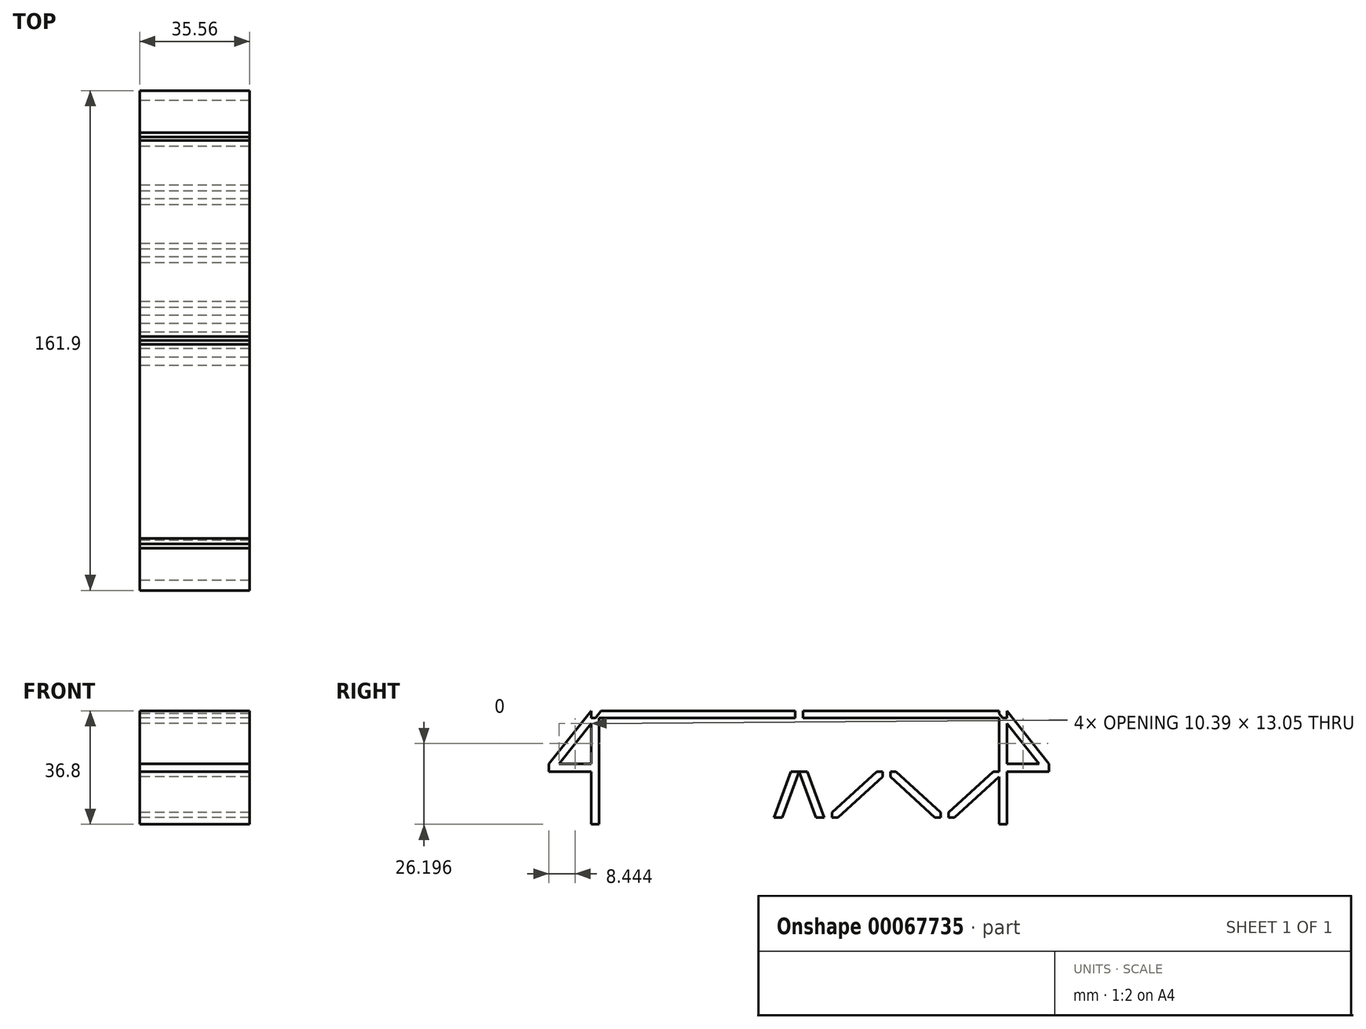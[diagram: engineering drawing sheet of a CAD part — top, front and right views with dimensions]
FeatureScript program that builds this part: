
annotation { "Feature Type Name" : "Feature", "Feature Type Description" : "" }
export const myFeature = defineFeature(function(context is Context, id is Id, definition is map)
    precondition{}
    {
        {
            var Q0;
            Q0=qCreatedBy(makeId("Right.planeOp"),FACE);
            var sketch = newSketch(context, id + "F0", { "sketchPlane" : qUnion([Q0])});
            skLineSegment(sketch, "E0.bottom", {"start": v(-67.31, 18.4) * mm, "end": v(67.3, 18.4) * mm});
            skLineSegment(sketch, "E0.top", {"start": v(-80.95, -18.4) * mm, "end": v(80.95, -18.4) * mm});
            skLineSegment(sketch, "E0.left", {"start": v(-80.95, 1.27) * mm, "end": v(-80.95, -18.4) * mm});
            skLineSegment(sketch, "E0.right", {"start": v(80.95, 1.27) * mm, "end": v(80.95, -18.4) * mm});
            skLineSegment(sketch, "E1.1", {"start": v(-78.4, 4.46) * mm, "end": v(-78.4, -16.22) * mm});
            skLineSegment(sketch, "E1.2", {"start": v(-78.4, -16.22) * mm, "end": v(78.4, -16.22) * mm});
            skLineSegment(sketch, "E1.3", {"start": v(78.4, 4.46) * mm, "end": v(78.4, -16.22) * mm});
            skLineSegment(sketch, "E2.rect.bottom", {"start": v(80.95, 1.27) * mm, "end": v(-80.95, 1.27) * mm});
            skLineSegment(sketch, "E2.rect.top", {"start": v(80.95, -1.27) * mm, "end": v(-80.95, -1.27) * mm});
            skLineSegment(sketch, "E2.rect.left", {"start": v(80.95, 1.27) * mm, "end": v(80.95, -1.27) * mm});
            skLineSegment(sketch, "E2.rect.right", {"start": v(-80.95, 1.27) * mm, "end": v(-80.95, -1.27) * mm});
            skPoint(sketch, "E2.rect.middle", {"position": v(0, 0) * mm});
            skLineSegment(sketch, "E3.rect.bottom", {"start": v(1.27, 18.4) * mm, "end": v(-1.27, 18.4) * mm});
            skLineSegment(sketch, "E3.rect.top", {"start": v(1.27, 1.27) * mm, "end": v(-1.27, 1.27) * mm});
            skLineSegment(sketch, "E3.rect.left", {"start": v(1.27, 18.4) * mm, "end": v(1.27, 1.27) * mm});
            skLineSegment(sketch, "E3.rect.right", {"start": v(-1.27, 18.4) * mm, "end": v(-1.27, 1.27) * mm});
            skPoint(sketch, "E3.rect.middle", {"position": v(0, 9.83) * mm});
            skPoint(sketch, "E3.rect.middle.positionSnap0", {"position": v(0, 1.27) * mm});
            skPoint(sketch, "E3.rect.centerSnap0", {"position": v(0, 1.27) * mm});
            skLineSegment(sketch, "E4.rect.bottom", {"start": v(67.3, 18.4) * mm, "end": v(64.77, 18.4) * mm});
            skLineSegment(sketch, "E4.rect.top", {"start": v(67.3, -18.4) * mm, "end": v(64.77, -18.4) * mm});
            skLineSegment(sketch, "E4.rect.left", {"start": v(67.3, 18.4) * mm, "end": v(67.3, -18.4) * mm});
            skLineSegment(sketch, "E4.rect.right", {"start": v(64.77, 18.4) * mm, "end": v(64.77, -18.4) * mm});
            skPoint(sketch, "E4.rect.middle", {"position": v(66.04, 0) * mm});
            skLineSegment(sketch, "E5.rect.bottom", {"start": v(-64.77, 18.4) * mm, "end": v(-67.31, 18.4) * mm});
            skLineSegment(sketch, "E5.rect.top", {"start": v(-64.77, -18.4) * mm, "end": v(-67.31, -18.4) * mm});
            skLineSegment(sketch, "E5.rect.left", {"start": v(-64.77, 18.4) * mm, "end": v(-64.77, -18.4) * mm});
            skLineSegment(sketch, "E5.rect.right", {"start": v(-67.31, 18.4) * mm, "end": v(-67.31, -18.4) * mm});
            skPoint(sketch, "E5.rect.middle", {"position": v(-66.04, 0) * mm});
            skLineSegment(sketch, "E6.bottom", {"start": v(-48.44, -1.27) * mm, "end": v(-45.9, -1.27) * mm});
            skLineSegment(sketch, "E6.top", {"start": v(-48.44, -16.22) * mm, "end": v(-45.9, -16.22) * mm});
            skLineSegment(sketch, "E6.left", {"start": v(-48.44, -1.27) * mm, "end": v(-48.44, -16.22) * mm});
            skLineSegment(sketch, "E6.right", {"start": v(-45.9, -1.27) * mm, "end": v(-45.9, -16.22) * mm});
            skLineSegment(sketch, "E7.bottom", {"start": v(-29.57, -1.27) * mm, "end": v(-27.03, -1.27) * mm});
            skLineSegment(sketch, "E7.top", {"start": v(-29.57, -16.22) * mm, "end": v(-27.03, -16.22) * mm});
            skLineSegment(sketch, "E7.left", {"start": v(-29.57, -1.27) * mm, "end": v(-29.57, -16.22) * mm});
            skLineSegment(sketch, "E7.right", {"start": v(-27.03, -1.27) * mm, "end": v(-27.03, -16.22) * mm});
            skLineSegment(sketch, "E8.bottom", {"start": v(-10.7, -1.27) * mm, "end": v(-8.15, -1.27) * mm});
            skLineSegment(sketch, "E8.top", {"start": v(-10.7, -16.22) * mm, "end": v(-8.15, -16.22) * mm});
            skLineSegment(sketch, "E8.left", {"start": v(-10.7, -1.27) * mm, "end": v(-10.7, -16.22) * mm});
            skLineSegment(sketch, "E8.right", {"start": v(-8.15, -1.27) * mm, "end": v(-8.15, -16.22) * mm});
            skLineSegment(sketch, "E9.bottom", {"start": v(8.15, -1.27) * mm, "end": v(10.7, -1.27) * mm});
            skLineSegment(sketch, "E9.top", {"start": v(8.15, -16.22) * mm, "end": v(10.7, -16.22) * mm});
            skLineSegment(sketch, "E9.left", {"start": v(8.15, -1.27) * mm, "end": v(8.15, -16.22) * mm});
            skLineSegment(sketch, "E9.right", {"start": v(10.7, -1.27) * mm, "end": v(10.7, -16.22) * mm});
            skLineSegment(sketch, "E10.bottom", {"start": v(27.03, -1.27) * mm, "end": v(29.57, -1.27) * mm});
            skLineSegment(sketch, "E10.top", {"start": v(27.03, -16.22) * mm, "end": v(29.57, -16.22) * mm});
            skLineSegment(sketch, "E10.left", {"start": v(27.03, -1.27) * mm, "end": v(27.03, -16.22) * mm});
            skLineSegment(sketch, "E10.right", {"start": v(29.57, -1.27) * mm, "end": v(29.57, -16.22) * mm});
            skLineSegment(sketch, "E11.bottom", {"start": v(45.9, -1.27) * mm, "end": v(48.44, -1.27) * mm});
            skLineSegment(sketch, "E11.top", {"start": v(45.9, -16.22) * mm, "end": v(48.44, -16.22) * mm});
            skLineSegment(sketch, "E11.left", {"start": v(45.9, -1.27) * mm, "end": v(45.9, -16.22) * mm});
            skLineSegment(sketch, "E11.right", {"start": v(48.44, -1.27) * mm, "end": v(48.44, -16.22) * mm});
            skLineSegment(sketch, "E12", {"start": v(0, 19.15) * mm, "end": v(0, -18.4) * mm, "construction": true});
            skLineSegment(sketch, "E13", {"start": v(-80.95, 0.2) * mm, "end": v(80.95, 0.2) * mm, "construction": true});
            skLineSegment(sketch, "E14", {"start": v(67.31, 18.4) * mm, "end": v(80.95, 1.27) * mm});
            skLineSegment(sketch, "E15", {"start": v(64.06, 18.4) * mm, "end": v(79.73, -1.27) * mm});
            skLineSegment(sketch, "E16", {"start": v(-67.31, 18.4) * mm, "end": v(-80.95, 1.27) * mm});
            skLineSegment(sketch, "E17", {"start": v(-64.06, 18.4) * mm, "end": v(-79.73, -1.27) * mm});
            skLineSegment(sketch, "E18.trimOffspring", {"start": v(-69.13, 16.12) * mm, "end": v(67.3, 16.12) * mm});
            skLineSegment(sketch, "E19", {"start": v(0, -1.27) * mm, "end": v(-5.45, -16.22) * mm});
            skLineSegment(sketch, "E20", {"start": v(-2.7, -1.27) * mm, "end": v(-8.15, -16.22) * mm});
            skLineSegment(sketch, "E21", {"start": v(0, -1.27) * mm, "end": v(5.45, -16.22) * mm});
            skLineSegment(sketch, "E22", {"start": v(2.7, -1.27) * mm, "end": v(8.15, -16.22) * mm});
            skLineSegment(sketch, "E23.0", {"start": v(27.03, -3) * mm, "end": v(12.57, -16.22) * mm});
            skLineSegment(sketch, "E24.0", {"start": v(25.14, -1.27) * mm, "end": v(10.7, -14.5) * mm});
            skLineSegment(sketch, "E25.0", {"start": v(31.45, -1.27) * mm, "end": v(45.9, -14.5) * mm});
            skLineSegment(sketch, "E26.0", {"start": v(29.57, -3) * mm, "end": v(44.02, -16.22) * mm});
            skLineSegment(sketch, "E27.0", {"start": v(50.32, -16.22) * mm, "end": v(64.77, -3) * mm});
            skLineSegment(sketch, "E28.0", {"start": v(48.44, -14.5) * mm, "end": v(62.89, -1.27) * mm});
            skPoint(sketch, "E29.startSnap0", {"position": v(67.3, 0) * mm});
            skLineSegment(sketch, "E30.0", {"start": v(67.31, -3.4) * mm, "end": v(76.8, -16.22) * mm});
            skLineSegment(sketch, "E31.0", {"start": v(68.9, -1.27) * mm, "end": v(78.4, -14) * mm});
            skSolve(sketch);
        }
        {
            var Q0;
            {var subQ4=sQuery(id+"F0.wireOp",EDGE,"E27.0");Q0=makeQuery(id+"F0.imprint","IMPRINT",FACE,{"disambiguationData":[TD([[makeQuery(id+"F0.imprint","IMPRINT",EDGE,{"derivedFrom":subQ4}),1.0]])]});}
            var Q1;
            {var subQ2=sQuery(id+"F0.wireOp",EDGE,"E21");Q1=makeQuery(id+"F0.imprint","IMPRINT",FACE,{"disambiguationData":[TD([[makeQuery(id+"F0.imprint","IMPRINT",EDGE,{"derivedFrom":subQ2}),1.0]])]});}
            var Q2;
            {var subQ7=sQuery(id+"F0.wireOp",EDGE,"E0.right");Q2=makeQuery(id+"F0.imprint","IMPRINT",FACE,{"disambiguationData":[TD([[makeQuery(id+"F0.imprint","IMPRINT",EDGE,{"derivedFrom":subQ7}),-1.0]])]});}
            var Q3;
            Q3=makeQuery(id+"F0.imprint","IMPRINT",FACE,{"disambiguationData":[TD([[makeQuery(id+"F0.imprint","IMPRINT",EDGE,{"derivedFrom":sQuery(id+"F0.wireOp",EDGE,"E7.bottom")}),-1.0]])]});
            var Q4;
            {var subQ2=sQuery(id+"F0.wireOp",EDGE,"E19");Q4=makeQuery(id+"F0.imprint","IMPRINT",FACE,{"disambiguationData":[TD([[makeQuery(id+"F0.imprint","IMPRINT",EDGE,{"derivedFrom":subQ2}),-1.0]])]});}
            var Q5;
            {var subQ1=sQuery(id+"F0.wireOp",EDGE,"E1.3");var subQ8=sQuery(id+"F0.wireOp",EDGE,"E14");var subQ10=makeQuery(id+"F0.imprint","INTERSECT",VERTEX,{"derivedFrom":[subQ1,subQ8]});Q5=makeQuery(id+"F0.imprint","IMPRINT",FACE,{"disambiguationData":[TD([[makeQuery(id+"F0.imprint","IMPRINT",EDGE,{"disambiguationData":[TD([[subQ10,-1.0]])],"derivedFrom":subQ1}),-1.0]])]});}
            var Q6;
            {var subQ0=sQuery(id+"F0.wireOp",EDGE,"E16");var subQ1=sQuery(id+"F0.wireOp",EDGE,"E1.1");var subQ2=makeQuery(id+"F0.imprint","INTERSECT",VERTEX,{"derivedFrom":[subQ1,subQ0]});Q6=makeQuery(id+"F0.imprint","IMPRINT",FACE,{"disambiguationData":[TD([[makeQuery(id+"F0.imprint","IMPRINT",EDGE,{"disambiguationData":[TD([[subQ2,-1.0]])],"derivedFrom":subQ1}),1.0]])]});}
            var Q7;
            {var subQ7=sQuery(id+"F0.wireOp",EDGE,"E25.0");Q7=makeQuery(id+"F0.imprint","IMPRINT",FACE,{"disambiguationData":[TD([[makeQuery(id+"F0.imprint","IMPRINT",EDGE,{"derivedFrom":subQ7}),-1.0]])]});}
            var Q8;
            {var subQ0=sQuery(id+"F0.wireOp",EDGE,"E17");var subQ3=sQuery(id+"F0.wireOp",EDGE,"E5.rect.left");var subQ4=makeQuery(id+"F0.imprint","INTERSECT",VERTEX,{"derivedFrom":[subQ3,subQ0]});Q8=makeQuery(id+"F0.imprint","IMPRINT",FACE,{"disambiguationData":[TD([[makeQuery(id+"F0.imprint","IMPRINT",EDGE,{"disambiguationData":[TD([[subQ4,-1.0]])],"derivedFrom":subQ3}),1.0]])]});}
            var Q9;
            Q9=makeQuery(id+"F0.imprint","IMPRINT",FACE,{"disambiguationData":[TD([[makeQuery(id+"F0.imprint","IMPRINT",EDGE,{"derivedFrom":sQuery(id+"F0.wireOp",EDGE,"E8.bottom")}),-1.0]])]});
            var Q10;
            {var subQ0=sQuery(id+"F0.wireOp",EDGE,"E3.rect.top");Q10=makeQuery(id+"F0.imprint","IMPRINT",FACE,{"disambiguationData":[TD([[makeQuery(id+"F0.imprint","IMPRINT",EDGE,{"derivedFrom":subQ0}),-1.0]])]});}
            var Q11;
            {var subQ7=sQuery(id+"F0.wireOp",EDGE,"E0.left");Q11=makeQuery(id+"F0.imprint","IMPRINT",FACE,{"disambiguationData":[TD([[makeQuery(id+"F0.imprint","IMPRINT",EDGE,{"derivedFrom":subQ7}),1.0]])]});}
            var Q12;
            Q12=makeQuery(id+"F0.imprint","IMPRINT",FACE,{"disambiguationData":[TD([[makeQuery(id+"F0.imprint","IMPRINT",EDGE,{"derivedFrom":sQuery(id+"F0.wireOp",EDGE,"E6.bottom")}),-1.0]])]});
            var Q13;
            {var subQ15=sQuery(id+"F0.wireOp",EDGE,"E6.top");Q13=makeQuery(id+"F0.imprint","IMPRINT",FACE,{"disambiguationData":[TD([[makeQuery(id+"F0.imprint","IMPRINT",EDGE,{"derivedFrom":subQ15}),-1.0]])]});}
            var Q14;
            {var subQ1=sQuery(id+"F0.wireOp",EDGE,"E9.bottom");Q14=makeQuery(id+"F0.imprint","IMPRINT",FACE,{"disambiguationData":[TD([[makeQuery(id+"F0.imprint","IMPRINT",EDGE,{"derivedFrom":subQ1}),-1.0]])]});}
            var Q15;
            {var subQ4=sQuery(id+"F0.wireOp",EDGE,"E11.bottom");Q15=makeQuery(id+"F0.imprint","IMPRINT",FACE,{"disambiguationData":[TD([[makeQuery(id+"F0.imprint","IMPRINT",EDGE,{"derivedFrom":subQ4}),-1.0]])]});}
            var Q16;
            {var subQ0=sQuery(id+"F0.wireOp",EDGE,"E4.rect.right");var subQ5=sQuery(id+"F0.wireOp",EDGE,"E1.2");var subQ8=makeQuery(id+"F0.imprint","INTERSECT",VERTEX,{"derivedFrom":[subQ5,subQ0]});Q16=makeQuery(id+"F0.imprint","IMPRINT",FACE,{"disambiguationData":[TD([[makeQuery(id+"F0.imprint","IMPRINT",EDGE,{"disambiguationData":[TD([[subQ8,-1.0]])],"derivedFrom":subQ5}),1.0]])]});}
            var Q17;
            {var subQ5=sQuery(id+"F0.wireOp",EDGE,"E2.rect.bottom");var subQ7=sQuery(id+"F0.wireOp",EDGE,"E5.rect.left");var subQ8=makeQuery(id+"F0.imprint","INTERSECT",VERTEX,{"derivedFrom":[subQ5,subQ7]});Q17=makeQuery(id+"F0.imprint","IMPRINT",FACE,{"disambiguationData":[TD([[makeQuery(id+"F0.imprint","IMPRINT",EDGE,{"disambiguationData":[TD([[subQ8,-1.0]])],"derivedFrom":subQ5}),-1.0]])]});}
            var Q18;
            {var subQ0=sQuery(id+"F0.wireOp",EDGE,"E14");var subQ1=sQuery(id+"F0.wireOp",EDGE,"E1.3");var subQ2=makeQuery(id+"F0.imprint","INTERSECT",VERTEX,{"derivedFrom":[subQ1,subQ0]});Q18=makeQuery(id+"F0.imprint","IMPRINT",FACE,{"disambiguationData":[TD([[makeQuery(id+"F0.imprint","IMPRINT",EDGE,{"disambiguationData":[TD([[subQ2,-1.0]])],"derivedFrom":subQ1}),1.0]])]});}
            var Q19;
            {var subQ0=sQuery(id+"F0.wireOp",EDGE,"E16");var subQ1=sQuery(id+"F0.wireOp",EDGE,"E1.1");var subQ2=makeQuery(id+"F0.imprint","INTERSECT",VERTEX,{"derivedFrom":[subQ1,subQ0]});Q19=makeQuery(id+"F0.imprint","IMPRINT",FACE,{"disambiguationData":[TD([[makeQuery(id+"F0.imprint","IMPRINT",EDGE,{"disambiguationData":[TD([[subQ2,-1.0]])],"derivedFrom":subQ1}),-1.0]])]});}
            var Q20;
            {var subQ0=sQuery(id+"F0.wireOp",EDGE,"E5.rect.right");var subQ1=sQuery(id+"F0.wireOp",EDGE,"E1.2");var subQ2=makeQuery(id+"F0.imprint","INTERSECT",VERTEX,{"derivedFrom":[subQ1,subQ0]});Q20=makeQuery(id+"F0.imprint","IMPRINT",FACE,{"disambiguationData":[TD([[makeQuery(id+"F0.imprint","IMPRINT",EDGE,{"disambiguationData":[TD([[subQ2,-1.0]])],"derivedFrom":subQ1}),1.0]])]});}
            var Q21;
            {var subQ4=sQuery(id+"F0.wireOp",EDGE,"E10.bottom");Q21=makeQuery(id+"F0.imprint","IMPRINT",FACE,{"disambiguationData":[TD([[makeQuery(id+"F0.imprint","IMPRINT",EDGE,{"derivedFrom":subQ4}),-1.0]])]});}
            var Q22;
            {var subQ3=sQuery(id+"F0.wireOp",EDGE,"E23.0");Q22=makeQuery(id+"F0.imprint","IMPRINT",FACE,{"disambiguationData":[TD([[makeQuery(id+"F0.imprint","IMPRINT",EDGE,{"derivedFrom":subQ3}),-1.0]])]});}
            var Q23;
            {var subQ0=sQuery(id+"F0.wireOp",EDGE,"E18.trimOffspring");var subQ1=sQuery(id+"F0.wireOp",EDGE,"E4.rect.left");var subQ2=makeQuery(id+"F0.imprint","INTERSECT",VERTEX,{"derivedFrom":[subQ1,subQ0]});Q23=makeQuery(id+"F0.imprint","IMPRINT",FACE,{"disambiguationData":[TD([[makeQuery(id+"F0.imprint","IMPRINT",EDGE,{"disambiguationData":[TD([[subQ2,-1.0]])],"derivedFrom":subQ1}),-1.0]])]});}
            var Q24;
            {var subQ5=sQuery(id+"F0.wireOp",EDGE,"E1.3");var subQ7=sQuery(id+"F0.wireOp",EDGE,"E15");var subQ8=makeQuery(id+"F0.imprint","INTERSECT",VERTEX,{"derivedFrom":[subQ5,subQ7]});Q24=makeQuery(id+"F0.imprint","IMPRINT",FACE,{"disambiguationData":[TD([[makeQuery(id+"F0.imprint","IMPRINT",EDGE,{"disambiguationData":[TD([[subQ8,-1.0]])],"derivedFrom":subQ5}),-1.0]])]});}
            var Q25;
            {var subQ5=sQuery(id+"F0.wireOp",EDGE,"E1.1");var subQ7=sQuery(id+"F0.wireOp",EDGE,"E17");var subQ9=makeQuery(id+"F0.imprint","INTERSECT",VERTEX,{"derivedFrom":[subQ5,subQ7]});Q25=makeQuery(id+"F0.imprint","IMPRINT",FACE,{"disambiguationData":[TD([[makeQuery(id+"F0.imprint","IMPRINT",EDGE,{"disambiguationData":[TD([[subQ9,-1.0]])],"derivedFrom":subQ5}),1.0]])]});}
            var Q26;
            {var subQ0=sQuery(id+"F0.wireOp",EDGE,"E3.rect.bottom");Q26=makeQuery(id+"F0.imprint","IMPRINT",FACE,{"disambiguationData":[TD([[makeQuery(id+"F0.imprint","IMPRINT",EDGE,{"derivedFrom":subQ0}),1.0]])]});}
            var Q27;
            {var subQ0=sQuery(id+"F0.wireOp",EDGE,"E18.trimOffspring");var subQ1=sQuery(id+"F0.wireOp",EDGE,"E5.rect.right");var subQ2=makeQuery(id+"F0.imprint","INTERSECT",VERTEX,{"derivedFrom":[subQ1,subQ0]});Q27=makeQuery(id+"F0.imprint","IMPRINT",FACE,{"disambiguationData":[TD([[makeQuery(id+"F0.imprint","IMPRINT",EDGE,{"disambiguationData":[TD([[subQ2,-1.0]])],"derivedFrom":subQ1}),1.0]])]});}
            var Q28;
            {var subQ0=sQuery(id+"F0.wireOp",EDGE,"E5.rect.left");var subQ1=sQuery(id+"F0.wireOp",EDGE,"E2.rect.bottom");var subQ2=makeQuery(id+"F0.imprint","INTERSECT",VERTEX,{"derivedFrom":[subQ1,subQ0]});Q28=makeQuery(id+"F0.imprint","IMPRINT",FACE,{"disambiguationData":[TD([[makeQuery(id+"F0.imprint","IMPRINT",EDGE,{"disambiguationData":[TD([[subQ2,-1.0]])],"derivedFrom":subQ1}),1.0]])]});}
            var Q29;
            {var subQ0=sQuery(id+"F0.wireOp",EDGE,"E4.rect.right");var subQ1=sQuery(id+"F0.wireOp",EDGE,"E0.top");var subQ2=makeQuery(id+"F0.imprint","INTERSECT",VERTEX,{"derivedFrom":[subQ1,subQ0]});Q29=makeQuery(id+"F0.imprint","IMPRINT",FACE,{"disambiguationData":[TD([[makeQuery(id+"F0.imprint","IMPRINT",EDGE,{"disambiguationData":[TD([[subQ2,-1.0]])],"derivedFrom":subQ1}),1.0]])]});}
            var Q30;
            {var subQ0=sQuery(id+"F0.wireOp",EDGE,"E4.rect.left");var subQ1=sQuery(id+"F0.wireOp",EDGE,"E2.rect.bottom");var subQ2=makeQuery(id+"F0.imprint","INTERSECT",VERTEX,{"derivedFrom":[subQ1,subQ0]});Q30=makeQuery(id+"F0.imprint","IMPRINT",FACE,{"disambiguationData":[TD([[makeQuery(id+"F0.imprint","IMPRINT",EDGE,{"disambiguationData":[TD([[subQ2,-1.0]])],"derivedFrom":subQ1}),1.0]])]});}
            var Q31;
            {var subQ0=sQuery(id+"F0.wireOp",EDGE,"E5.rect.right");var subQ1=sQuery(id+"F0.wireOp",EDGE,"E0.top");var subQ2=makeQuery(id+"F0.imprint","INTERSECT",VERTEX,{"derivedFrom":[subQ1,subQ0]});Q31=makeQuery(id+"F0.imprint","IMPRINT",FACE,{"disambiguationData":[TD([[makeQuery(id+"F0.imprint","IMPRINT",EDGE,{"disambiguationData":[TD([[subQ2,-1.0]])],"derivedFrom":subQ1}),1.0]])]});}
            var Q32;
            {var subQ6=sQuery(id+"F0.wireOp",EDGE,"E3.rect.top");Q32=makeQuery(id+"F0.imprint","IMPRINT",FACE,{"disambiguationData":[TD([[makeQuery(id+"F0.imprint","IMPRINT",EDGE,{"derivedFrom":subQ6}),1.0]])]});}
            var Q33;
            {var subQ0=sQuery(id+"F0.wireOp",EDGE,"E2.rect.left");Q33=makeQuery(id+"F0.imprint","IMPRINT",FACE,{"disambiguationData":[TD([[makeQuery(id+"F0.imprint","IMPRINT",EDGE,{"derivedFrom":subQ0}),-1.0]])]});}
            var Q34;
            {var subQ0=sQuery(id+"F0.wireOp",EDGE,"E17");var subQ1=sQuery(id+"F0.wireOp",EDGE,"E5.rect.left");var subQ2=makeQuery(id+"F0.imprint","INTERSECT",VERTEX,{"derivedFrom":[subQ1,subQ0]});Q34=makeQuery(id+"F0.imprint","IMPRINT",FACE,{"disambiguationData":[TD([[makeQuery(id+"F0.imprint","IMPRINT",EDGE,{"disambiguationData":[TD([[subQ2,-1.0]])],"derivedFrom":subQ1}),-1.0]])]});}
            var Q35;
            {var subQ5=sQuery(id+"F0.wireOp",EDGE,"E4.rect.top");Q35=makeQuery(id+"F0.imprint","IMPRINT",FACE,{"disambiguationData":[TD([[makeQuery(id+"F0.imprint","IMPRINT",EDGE,{"derivedFrom":subQ5}),-1.0]])]});}
            var Q36;
            {var subQ5=sQuery(id+"F0.wireOp",EDGE,"E5.rect.top");Q36=makeQuery(id+"F0.imprint","IMPRINT",FACE,{"disambiguationData":[TD([[makeQuery(id+"F0.imprint","IMPRINT",EDGE,{"derivedFrom":subQ5}),-1.0]])]});}
            var Q37;
            {var subQ0=sQuery(id+"F0.wireOp",EDGE,"E15");var subQ1=sQuery(id+"F0.wireOp",EDGE,"E1.3");var subQ2=makeQuery(id+"F0.imprint","INTERSECT",VERTEX,{"derivedFrom":[subQ1,subQ0]});Q37=makeQuery(id+"F0.imprint","IMPRINT",FACE,{"disambiguationData":[TD([[makeQuery(id+"F0.imprint","IMPRINT",EDGE,{"disambiguationData":[TD([[subQ2,-1.0]])],"derivedFrom":subQ1}),1.0]])]});}
            var Q38;
            {var subQ6=sQuery(id+"F0.wireOp",EDGE,"E5.rect.bottom");Q38=makeQuery(id+"F0.imprint","IMPRINT",FACE,{"disambiguationData":[TD([[makeQuery(id+"F0.imprint","IMPRINT",EDGE,{"derivedFrom":subQ6}),1.0]])]});}
            var Q39;
            {var subQ0=sQuery(id+"F0.wireOp",EDGE,"E17");var subQ1=sQuery(id+"F0.wireOp",EDGE,"E1.1");var subQ2=makeQuery(id+"F0.imprint","INTERSECT",VERTEX,{"derivedFrom":[subQ1,subQ0]});Q39=makeQuery(id+"F0.imprint","IMPRINT",FACE,{"disambiguationData":[TD([[makeQuery(id+"F0.imprint","IMPRINT",EDGE,{"disambiguationData":[TD([[subQ2,-1.0]])],"derivedFrom":subQ1}),-1.0]])]});}
            var Q40;
            {var subQ0=sQuery(id+"F0.wireOp",EDGE,"E2.rect.bottom");var subQ1=sQuery(id+"F0.wireOp",EDGE,"E1.1");var subQ2=makeQuery(id+"F0.imprint","INTERSECT",VERTEX,{"derivedFrom":[subQ1,subQ0]});Q40=makeQuery(id+"F0.imprint","IMPRINT",FACE,{"disambiguationData":[TD([[makeQuery(id+"F0.imprint","IMPRINT",EDGE,{"disambiguationData":[TD([[subQ2,-1.0]])],"derivedFrom":subQ1}),1.0]])]});}
            var Q41;
            {var subQ0=sQuery(id+"F0.wireOp",EDGE,"E16");var subQ3=sQuery(id+"F0.wireOp",EDGE,"E18.trimOffspring");var subQ5=makeQuery(id+"F0.imprint","INTERSECT",VERTEX,{"derivedFrom":[subQ0,subQ3]});Q41=makeQuery(id+"F0.imprint","IMPRINT",FACE,{"disambiguationData":[TD([[makeQuery(id+"F0.imprint","IMPRINT",EDGE,{"disambiguationData":[TD([[subQ5,-1.0]])],"derivedFrom":subQ3}),1.0]])]});}
            var Q42;
            {var subQ1=sQuery(id+"F0.wireOp",EDGE,"E0.bottom");var subQ3=sQuery(id+"F0.wireOp",EDGE,"E15");var subQ4=makeQuery(id+"F0.imprint","INTERSECT",VERTEX,{"derivedFrom":[subQ1,subQ3]});Q42=makeQuery(id+"F0.imprint","IMPRINT",FACE,{"disambiguationData":[TD([[makeQuery(id+"F0.imprint","IMPRINT",EDGE,{"disambiguationData":[TD([[subQ4,-1.0]])],"derivedFrom":subQ3}),1.0]])]});}
            var Q43;
            {var subQ1=sQuery(id+"F0.wireOp",EDGE,"E4.rect.bottom");Q43=makeQuery(id+"F0.imprint","IMPRINT",FACE,{"disambiguationData":[TD([[makeQuery(id+"F0.imprint","IMPRINT",EDGE,{"derivedFrom":subQ1}),1.0]])]});}
            var Q44;
            {var subQ0=sQuery(id+"F0.wireOp",EDGE,"E2.rect.bottom");var subQ1=sQuery(id+"F0.wireOp",EDGE,"E1.3");var subQ2=makeQuery(id+"F0.imprint","INTERSECT",VERTEX,{"derivedFrom":[subQ1,subQ0]});Q44=makeQuery(id+"F0.imprint","IMPRINT",FACE,{"disambiguationData":[TD([[makeQuery(id+"F0.imprint","IMPRINT",EDGE,{"disambiguationData":[TD([[subQ2,-1.0]])],"derivedFrom":subQ1}),-1.0]])]});}
            var Q45;
            {var subQ0=sQuery(id+"F0.wireOp",EDGE,"E15");var subQ1=sQuery(id+"F0.wireOp",EDGE,"E4.rect.right");var subQ2=makeQuery(id+"F0.imprint","INTERSECT",VERTEX,{"derivedFrom":[subQ1,subQ0]});Q45=makeQuery(id+"F0.imprint","IMPRINT",FACE,{"disambiguationData":[TD([[makeQuery(id+"F0.imprint","IMPRINT",EDGE,{"disambiguationData":[TD([[subQ2,-1.0]])],"derivedFrom":subQ1}),1.0]])]});}
            var Q46;
            {var subQ0=sQuery(id+"F0.wireOp",EDGE,"E2.rect.right");Q46=makeQuery(id+"F0.imprint","IMPRINT",FACE,{"disambiguationData":[TD([[makeQuery(id+"F0.imprint","IMPRINT",EDGE,{"derivedFrom":subQ0}),1.0]])]});}
            var Q47;
            {var subQ0=sQuery(id+"F0.wireOp",EDGE,"E15");var subQ3=sQuery(id+"F0.wireOp",EDGE,"E4.rect.right");var subQ4=makeQuery(id+"F0.imprint","INTERSECT",VERTEX,{"derivedFrom":[subQ3,subQ0]});Q47=makeQuery(id+"F0.imprint","IMPRINT",FACE,{"disambiguationData":[TD([[makeQuery(id+"F0.imprint","IMPRINT",EDGE,{"disambiguationData":[TD([[subQ4,-1.0]])],"derivedFrom":subQ3}),-1.0]])]});}
            var Q48;
            {var subQ1=sQuery(id+"F0.wireOp",EDGE,"E4.rect.left");var subQ5=sQuery(id+"F0.wireOp",EDGE,"E2.rect.bottom");var subQ6=makeQuery(id+"F0.imprint","INTERSECT",VERTEX,{"derivedFrom":[subQ5,subQ1]});Q48=makeQuery(id+"F0.imprint","IMPRINT",FACE,{"disambiguationData":[TD([[makeQuery(id+"F0.imprint","IMPRINT",EDGE,{"disambiguationData":[TD([[subQ6,-1.0]])],"derivedFrom":subQ5}),-1.0]])]});}
            extrude(context, id + "F1", {"entities" : qUnion([Q0, Q1, Q2, Q3, Q4, Q5, Q6, Q7, Q8, Q9, Q10, Q11, Q12, Q13, Q14, Q15, Q16, Q17, Q18, Q19, Q20, Q21, Q22, Q23, Q24, Q25, Q26, Q27, Q28, Q29, Q30, Q31, Q32, Q33, Q34, Q35, Q36, Q37, Q38, Q39, Q40, Q41, Q42, Q43, Q44, Q45, Q46, Q47, Q48]), "depth" : 35.56 * mm});
        }
    });
